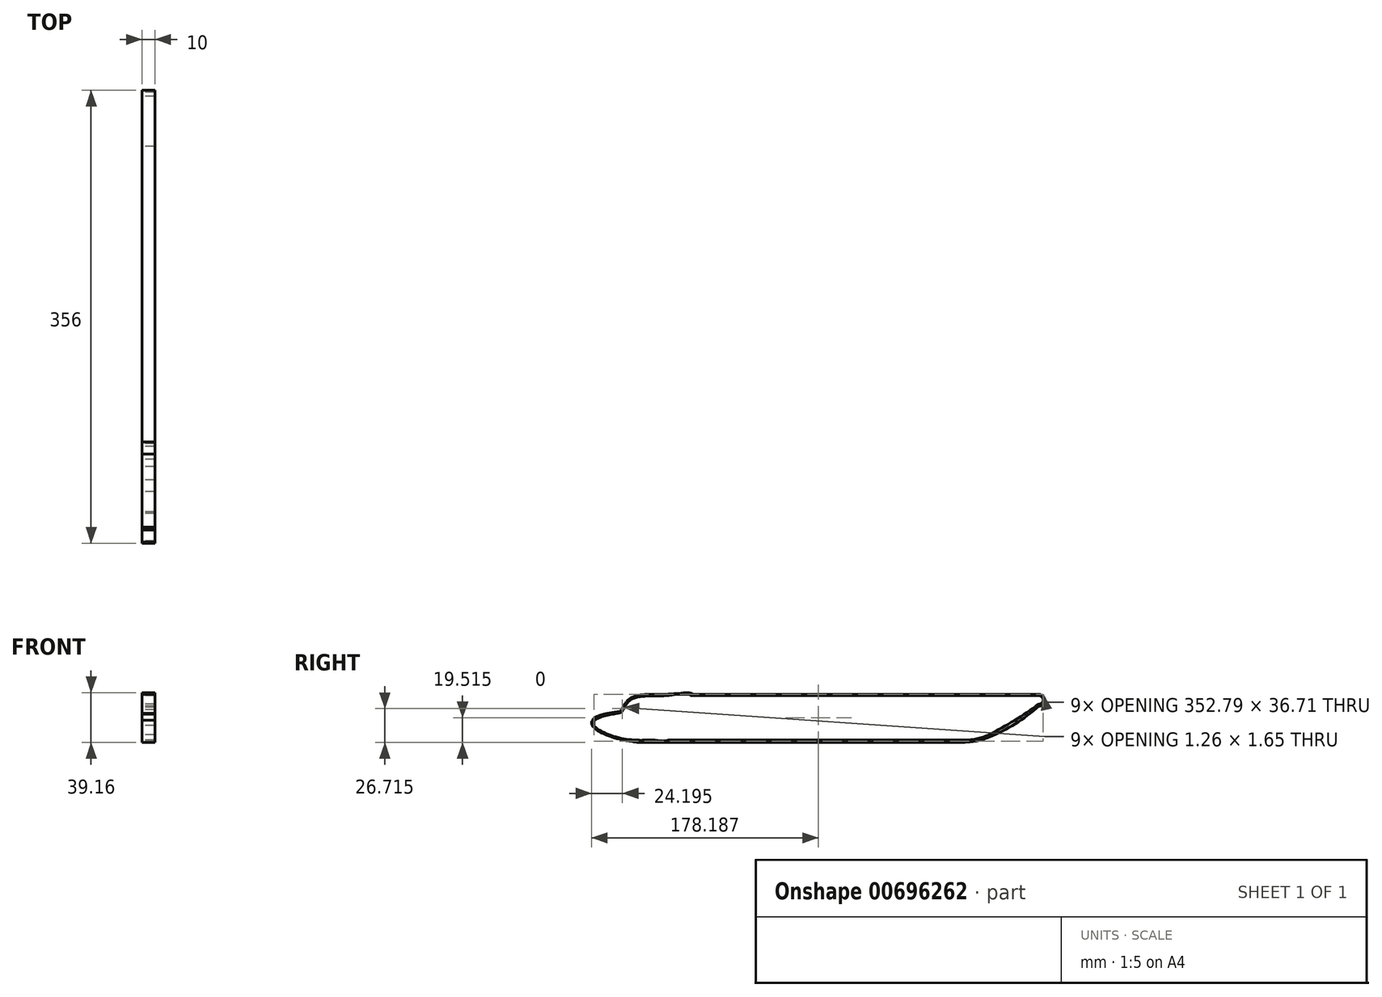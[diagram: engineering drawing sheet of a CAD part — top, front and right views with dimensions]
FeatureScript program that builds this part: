
annotation { "Feature Type Name" : "Feature", "Feature Type Description" : "" }
export const myFeature = defineFeature(function(context is Context, id is Id, definition is map)
    precondition{}
    {
        {
            var Q0;
            Q0=qCreatedBy(makeId("Right.planeOp"),FACE);
            var sketch = newSketch(context, id + "F0", { "sketchPlane" : qUnion([Q0])});
            skLineSegment(sketch, "E0.bottom", {"start": v(-67.14, 0.83) * mm, "end": v(67.14, 0.83) * mm});
            skLineSegment(sketch, "E0.top", {"start": v(-67.14, -0.83) * mm, "end": v(67.14, -0.83) * mm});
            skLineSegment(sketch, "E0.left", {"start": v(-67.14, 0.83) * mm, "end": v(-67.14, -0.83) * mm});
            skLineSegment(sketch, "E0.right", {"start": v(67.14, 0.83) * mm, "end": v(67.14, -0.83) * mm});
            skPoint(sketch, "E0.middle", {"position": v(0, 0) * mm});
            skFitSpline(sketch, "E1", {"points": [v(-67.14, -0.83) * mm, v(-85.43, 1.56) * mm, v(-103.1, 8.53) * mm, v(-107.43, 13.34) * mm, v(-106.6, 16.59) * mm, v(-97.33, 21.4) * mm, v(-87.42, 22.4) * mm, v(-84.78, 23.24) * mm, v(-82.4, 26.58) * mm, v(-67.14, 0.83) * mm, v(-67.14, -0.83) * mm]});
            skFitSpline(sketch, "E2", {"points": [v(-106.6, 16.59) * mm, v(-97.33, 21.4) * mm, v(-86.12, 23.24) * mm, v(-84.78, 23.9) * mm, v(-77.33, 33.68) * mm, v(-49.83, 36.9) * mm, v(-29.42, 35.83) * mm, v(-29.63, 23.24) * mm, v(-77.97, 6.4) * mm, v(-106.6, 16.59) * mm]});
            skLineSegment(sketch, "E3", {"start": v(-77.33, 33.68) * mm, "end": v(-84.78, 23.9) * mm});
            skFitSpline(sketch, "E4", {"points": [v(-67.14, 0.83) * mm, v(-85.43, 2.59) * mm, v(-102.42, 9.38) * mm, v(-106.22, 13.45) * mm, v(-105.78, 15.75) * mm, v(-97.28, 20) * mm, v(-86.12, 22.12) * mm, v(-83.2, 23.9) * mm, v(-76.39, 32.83) * mm, v(-49.83, 35.76) * mm, v(-34.7, 38.06) * mm, v(-26.82, 35.05) * mm, v(-43.37, 2.83) * mm, v(-57.8, 0.83) * mm, v(-67.14, 0.83) * mm]});
            skArc(sketch, "E5", {"start": v(-75.38, -0.35) * mm, "mid": v(-71.27, -0.7) * mm, "end": v(-67.14, -0.83) * mm});
            skLineSegment(sketch, "E6", {"start": v(-83.2, 23.9) * mm, "end": v(-76.39, 32.83) * mm});
            skLineSegment(sketch, "E7.left", {"start": v(67.14, -0.83) * mm, "end": v(67.14, 0.83) * mm});
            skPoint(sketch, "E7.right.end.orphan", {"position": v(162.32, 0.83) * mm});
            skLineSegment(sketch, "E8.bottom", {"start": v(67.14, -0.83) * mm, "end": v(184.2, -0.83) * mm});
            skLineSegment(sketch, "E8.top", {"start": v(67.14, 0.83) * mm, "end": v(184.2, 0.83) * mm});
            skLineSegment(sketch, "E8.right", {"start": v(184.2, -0.83) * mm, "end": v(184.2, 0.83) * mm});
            skLineSegment(sketch, "E9.bottom", {"start": v(-49.83, 36.9) * mm, "end": v(184.2, 36.9) * mm});
            skLineSegment(sketch, "E9.top", {"start": v(-49.83, 35.76) * mm, "end": v(184.2, 35.76) * mm});
            skLineSegment(sketch, "E9.left", {"start": v(-49.83, 36.9) * mm, "end": v(-49.83, 35.76) * mm});
            skLineSegment(sketch, "E9.right", {"start": v(184.2, 36.9) * mm, "end": v(184.2, 35.76) * mm});
            skLineSegment(sketch, "E10.bottom", {"start": v(184.2, 35.76) * mm, "end": v(243.74, 35.76) * mm});
            skLineSegment(sketch, "E10.top", {"start": v(184.2, 36.9) * mm, "end": v(243.74, 36.9) * mm});
            skLineSegment(sketch, "E10.left", {"start": v(184.2, 35.76) * mm, "end": v(184.2, 36.9) * mm});
            skLineSegment(sketch, "E10.right", {"start": v(243.74, 35.76) * mm, "end": v(243.74, 36.9) * mm});
            skLineSegment(sketch, "E11", {"start": v(243.74, 29.22) * mm, "end": v(243.74, 27.53) * mm});
            skArc(sketch, "E12", {"start": v(184.2, -0.83) * mm, "mid": v(194.55, 0.16) * mm, "end": v(204.53, 3.1) * mm});
            skArc(sketch, "E13", {"start": v(204.53, 3.1) * mm, "mid": v(225.16, 13.68) * mm, "end": v(243.74, 27.53) * mm});
            skArc(sketch, "E14", {"start": v(184.2, 0.83) * mm, "mid": v(194.58, 1.89) * mm, "end": v(204.53, 5.03) * mm});
            skArc(sketch, "E15", {"start": v(204.53, 5.03) * mm, "mid": v(224.6, 16.37) * mm, "end": v(243.74, 29.22) * mm});
            skArc(sketch, "E16", {"start": v(243.74, 27.53) * mm, "mid": v(248.43, 32.21) * mm, "end": v(243.74, 36.9) * mm});
            skArc(sketch, "E17", {"start": v(243.74, 29.22) * mm, "mid": v(247.01, 32.49) * mm, "end": v(243.74, 35.76) * mm});
            skLineSegment(sketch, "E18.bottom", {"start": v(-67.14, 0.83) * mm, "end": v(-53.07, 0.83) * mm});
            skLineSegment(sketch, "E18.top", {"start": v(-67.14, 1.8) * mm, "end": v(-53.07, 1.8) * mm});
            skLineSegment(sketch, "E18.left", {"start": v(-67.14, 0.83) * mm, "end": v(-67.14, 1.8) * mm});
            skLineSegment(sketch, "E18.right", {"start": v(-53.07, 0.83) * mm, "end": v(-53.07, 1.8) * mm});
            skLineSegment(sketch, "E19.bottom", {"start": v(-29.42, 0.83) * mm, "end": v(-13.04, 0.83) * mm});
            skLineSegment(sketch, "E19.top", {"start": v(-29.42, 1.8) * mm, "end": v(-13.04, 1.8) * mm});
            skLineSegment(sketch, "E19.left", {"start": v(-29.42, 0.83) * mm, "end": v(-29.42, 1.8) * mm});
            skLineSegment(sketch, "E19.right", {"start": v(-13.04, 0.83) * mm, "end": v(-13.04, 1.8) * mm});
            skLineSegment(sketch, "E20.bottom", {"start": v(6.5, 0.83) * mm, "end": v(23.1, 0.83) * mm});
            skLineSegment(sketch, "E20.top", {"start": v(6.5, 1.8) * mm, "end": v(23.1, 1.8) * mm});
            skLineSegment(sketch, "E20.left", {"start": v(6.5, 0.83) * mm, "end": v(6.5, 1.8) * mm});
            skLineSegment(sketch, "E20.right", {"start": v(23.1, 0.83) * mm, "end": v(23.1, 1.8) * mm});
            skLineSegment(sketch, "E21.bottom", {"start": v(41.13, 0.83) * mm, "end": v(58.4, 0.83) * mm});
            skLineSegment(sketch, "E21.top", {"start": v(41.13, 1.8) * mm, "end": v(58.4, 1.8) * mm});
            skLineSegment(sketch, "E21.left", {"start": v(41.13, 0.83) * mm, "end": v(41.13, 1.8) * mm});
            skLineSegment(sketch, "E21.right", {"start": v(58.4, 0.83) * mm, "end": v(58.4, 1.8) * mm});
            skLineSegment(sketch, "E22.bottom", {"start": v(76.45, 0.83) * mm, "end": v(93.55, 0.83) * mm});
            skLineSegment(sketch, "E22.top", {"start": v(76.45, 1.8) * mm, "end": v(93.55, 1.8) * mm});
            skLineSegment(sketch, "E22.left", {"start": v(76.45, 0.83) * mm, "end": v(76.45, 1.8) * mm});
            skLineSegment(sketch, "E22.right", {"start": v(93.55, 0.83) * mm, "end": v(93.55, 1.8) * mm});
            skLineSegment(sketch, "E23.bottom", {"start": v(108.37, 0.83) * mm, "end": v(125.48, 0.83) * mm});
            skLineSegment(sketch, "E23.top", {"start": v(108.37, 1.8) * mm, "end": v(125.48, 1.8) * mm});
            skLineSegment(sketch, "E23.left", {"start": v(108.37, 0.83) * mm, "end": v(108.37, 1.8) * mm});
            skLineSegment(sketch, "E23.right", {"start": v(125.48, 0.83) * mm, "end": v(125.48, 1.8) * mm});
            skLineSegment(sketch, "E24.bottom", {"start": v(141.82, 0.83) * mm, "end": v(156.83, 0.83) * mm});
            skLineSegment(sketch, "E24.top", {"start": v(141.82, 1.8) * mm, "end": v(156.83, 1.8) * mm});
            skLineSegment(sketch, "E24.left", {"start": v(141.82, 0.83) * mm, "end": v(141.82, 1.8) * mm});
            skLineSegment(sketch, "E24.right", {"start": v(156.83, 0.83) * mm, "end": v(156.83, 1.8) * mm});
            skLineSegment(sketch, "E25.bottom", {"start": v(176.02, 0.83) * mm, "end": v(184.2, 0.83) * mm});
            skLineSegment(sketch, "E25.top", {"start": v(176.02, 1.8) * mm, "end": v(184.2, 1.8) * mm});
            skLineSegment(sketch, "E25.left", {"start": v(176.02, 0.83) * mm, "end": v(176.02, 1.8) * mm});
            skLineSegment(sketch, "E25.right", {"start": v(184.2, 0.83) * mm, "end": v(184.2, 1.8) * mm});
            skLineSegment(sketch, "E26.bottom", {"start": v(-44.28, 0.83) * mm, "end": v(-36.32, 0.83) * mm});
            skLineSegment(sketch, "E26.top", {"start": v(-44.28, 1.8) * mm, "end": v(-36.32, 1.8) * mm});
            skLineSegment(sketch, "E26.left", {"start": v(-44.28, 0.83) * mm, "end": v(-44.28, 1.8) * mm});
            skLineSegment(sketch, "E26.right", {"start": v(-36.32, 0.83) * mm, "end": v(-36.32, 1.8) * mm});
            skLineSegment(sketch, "E27", {"start": v(231.82, 18.1) * mm, "end": v(231.82, 12.71) * mm});
            skLineSegment(sketch, "E28", {"start": v(-105.78, 15.75) * mm, "end": v(-105.78, 12.54) * mm});
            skLineSegment(sketch, "E29", {"start": v(-49.83, 36.9) * mm, "end": v(-49.83, 41.64) * mm});
            skLineSegment(sketch, "E30", {"start": v(184.2, -0.83) * mm, "end": v(184.2, -16.2) * mm});
            skSolve(sketch);
        }
        {
            var Q0;
            Q0 = qSketchRegion(id + "F0", true);
            var Q1;
            Q1=makeQuery(id+"F0.imprint","IMPRINT",FACE,{"disambiguationData":[TD([[makeQuery(id+"F0.imprint","IMPRINT",EDGE,{"derivedFrom":sQuery(id+"F0.wireOp",EDGE,"E26.bottom")}),1.0]])]});
            var Q2;
            Q2=makeQuery(id+"F0.imprint","IMPRINT",FACE,{"disambiguationData":[TD([[makeQuery(id+"F0.imprint","IMPRINT",EDGE,{"derivedFrom":sQuery(id+"F0.wireOp",EDGE,"E18.bottom")}),1.0]])]});
            var Q3;
            Q3=makeQuery(id+"F0.imprint","IMPRINT",FACE,{"disambiguationData":[TD([[makeQuery(id+"F0.imprint","IMPRINT",EDGE,{"derivedFrom":sQuery(id+"F0.wireOp",EDGE,"E19.bottom")}),1.0]])]});
            var Q4;
            Q4=makeQuery(id+"F0.imprint","IMPRINT",FACE,{"disambiguationData":[TD([[makeQuery(id+"F0.imprint","IMPRINT",EDGE,{"derivedFrom":sQuery(id+"F0.wireOp",EDGE,"E20.bottom")}),1.0]])]});
            var Q5;
            Q5=makeQuery(id+"F0.imprint","IMPRINT",FACE,{"disambiguationData":[TD([[makeQuery(id+"F0.imprint","IMPRINT",EDGE,{"derivedFrom":sQuery(id+"F0.wireOp",EDGE,"E21.bottom")}),1.0]])]});
            var Q6;
            Q6=makeQuery(id+"F0.imprint","IMPRINT",FACE,{"disambiguationData":[TD([[makeQuery(id+"F0.imprint","IMPRINT",EDGE,{"derivedFrom":sQuery(id+"F0.wireOp",EDGE,"E22.bottom")}),1.0]])]});
            var Q7;
            Q7=makeQuery(id+"F0.imprint","IMPRINT",FACE,{"disambiguationData":[TD([[makeQuery(id+"F0.imprint","IMPRINT",EDGE,{"derivedFrom":sQuery(id+"F0.wireOp",EDGE,"E23.bottom")}),1.0]])]});
            var Q8;
            Q8=makeQuery(id+"F0.imprint","IMPRINT",FACE,{"disambiguationData":[TD([[makeQuery(id+"F0.imprint","IMPRINT",EDGE,{"derivedFrom":sQuery(id+"F0.wireOp",EDGE,"E24.bottom")}),1.0]])]});
            var Q9;
            Q9=makeQuery(id+"F0.imprint","IMPRINT",FACE,{"disambiguationData":[TD([[makeQuery(id+"F0.imprint","IMPRINT",EDGE,{"derivedFrom":sQuery(id+"F0.wireOp",EDGE,"E25.bottom")}),1.0]])]});
            var Q10;
            {var subQ0=sQuery(id+"F0.wireOp",EDGE,"E28");Q10=makeQuery(id+"F0.imprint","IMPRINT",FACE,{"disambiguationData":[TD([[makeQuery(id+"F0.imprint","IMPRINT",EDGE,{"derivedFrom":subQ0}),-1.0]])]});}
            extrude(context, id + "F1", {"entities" : qUnion([Q0, Q1, Q2, Q3, Q4, Q5, Q6, Q7, Q8, Q9, Q10]), "depth" : 10 * mm, "offsetDistance" : 25 * mm});
        }
    });
